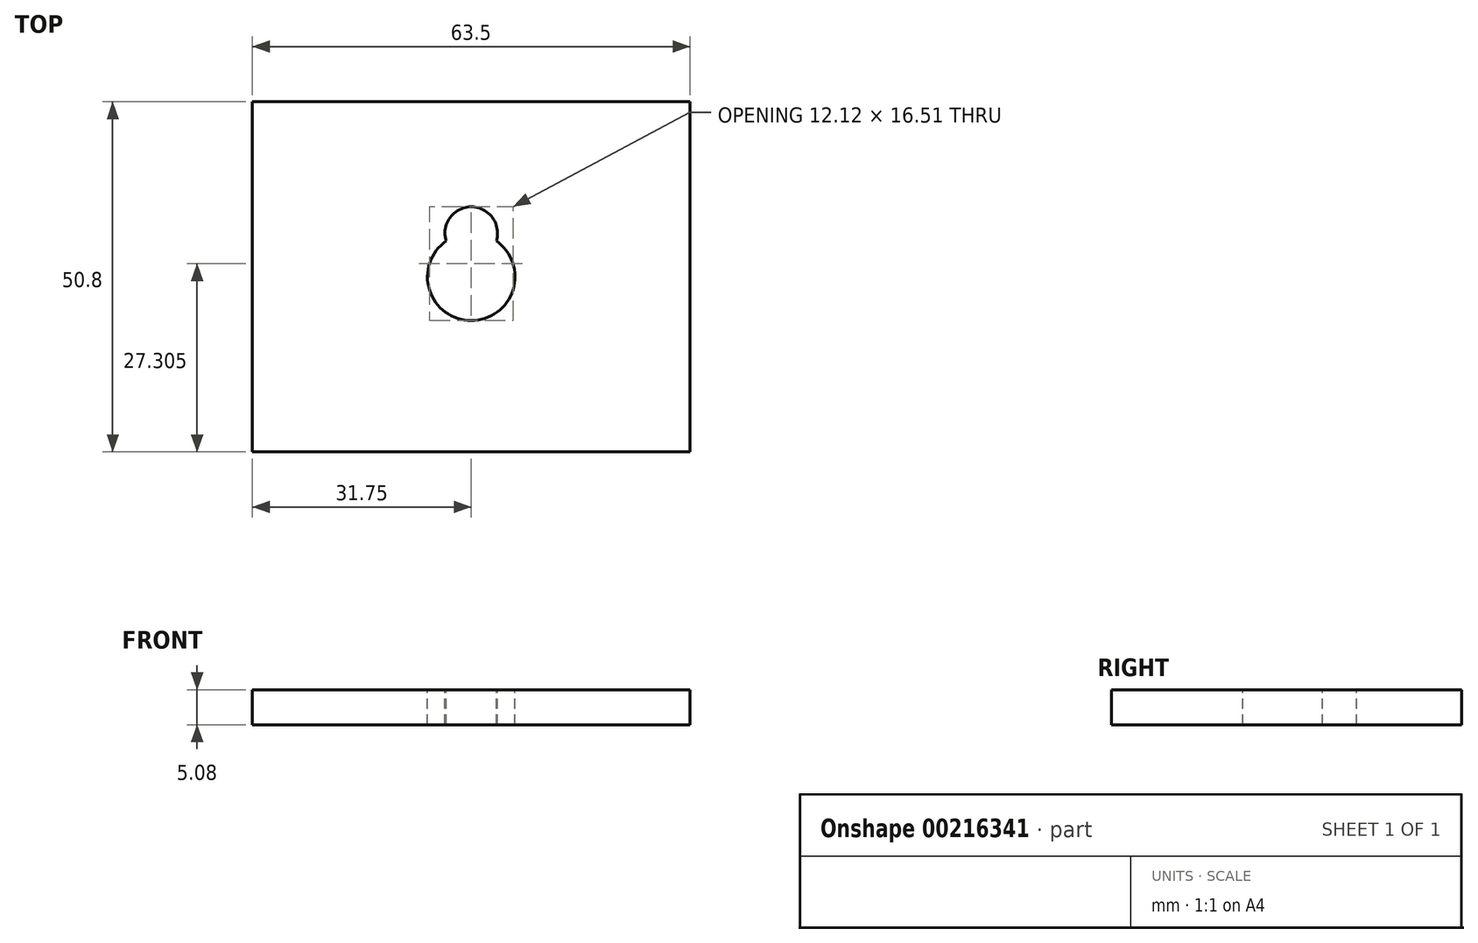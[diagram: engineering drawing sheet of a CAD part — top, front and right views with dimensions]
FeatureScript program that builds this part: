
annotation { "Feature Type Name" : "Feature", "Feature Type Description" : "" }
export const myFeature = defineFeature(function(context is Context, id is Id, definition is map)
    precondition{}
    {
        {
            var Q0;
            Q0=qCreatedBy(makeId("Top.planeOp"),FACE);
            var sketch = newSketch(context, id + "F0", { "sketchPlane" : qUnion([Q0])});
            skLineSegment(sketch, "E0.bottom", {"start": v(-31.75, 25.4) * mm, "end": v(31.75, 25.4) * mm});
            skLineSegment(sketch, "E0.top", {"start": v(-31.75, -25.4) * mm, "end": v(31.75, -25.4) * mm});
            skLineSegment(sketch, "E0.left", {"start": v(-31.75, 25.4) * mm, "end": v(-31.75, -25.4) * mm});
            skLineSegment(sketch, "E0.right", {"start": v(31.75, 25.4) * mm, "end": v(31.75, -25.4) * mm});
            skPoint(sketch, "E0.middle", {"position": v(0, 0) * mm});
            skSolve(sketch);
        }
        {
            var Q0;
            Q0=makeQuery(id+"F0.imprint","IMPRINT",FACE,{"disambiguationData":[TD([[makeQuery(id+"F0.imprint","IMPRINT",EDGE,{"derivedFrom":sQuery(id+"F0.wireOp",EDGE,"E0.bottom")}),-1.0]])]});
            extrude(context, id + "F1", {"entities" : qUnion([Q0]), "depth" : 5.08 * mm});
        }
        {
            var Q0;
            Q0=makeQuery(id+"F1.opExtrude","CAP_FACE",FACE,{"disambiguationData":[OSD([sQuery(id+"F0.wireOp",EDGE,"E0.bottom"),sQuery(id+"F0.wireOp",EDGE,"E0.top"),sQuery(id+"F0.wireOp",EDGE,"E0.left"),sQuery(id+"F0.wireOp",EDGE,"E0.right")])],"isStart":false});
            var sketch = newSketch(context, id + "F2", { "sketchPlane" : qUnion([Q0])});
            skCircle(sketch, "E1", {"center": v(0, 6.35) * mm, "radius": 3.81 * mm});
            skCircle(sketch, "E2", {"center": v(0, 0) * mm, "radius": 6.35 * mm});
            skSolve(sketch);
        }
        {
            var Q0;
            {var subQ0=sQuery(id+"F2.wireOp",EDGE,"E2");var subQ1=sQuery(id+"F2.wireOp",EDGE,"E1");var subQ2=makeQuery(id+"F2.imprint","INTERSECT",VERTEX,{"disambiguationData":[OD(0.0)],"derivedFrom":[subQ1,subQ0]});Q0=makeQuery(id+"F2.imprint","IMPRINT",FACE,{"disambiguationData":[TD([[makeQuery(id+"F2.imprint","IMPRINT",EDGE,{"disambiguationData":[TD([[subQ2,-1.0]])],"derivedFrom":subQ1}),-1.0]])]});}
            var Q1;
            {var subQ0=sQuery(id+"F2.wireOp",EDGE,"E2");var subQ1=sQuery(id+"F2.wireOp",EDGE,"E1");var subQ2=makeQuery(id+"F2.imprint","INTERSECT",VERTEX,{"disambiguationData":[OD(0.0)],"derivedFrom":[subQ1,subQ0]});Q1=makeQuery(id+"F2.imprint","IMPRINT",FACE,{"disambiguationData":[TD([[makeQuery(id+"F2.imprint","IMPRINT",EDGE,{"disambiguationData":[TD([[subQ2,1.0]])],"derivedFrom":subQ1}),1.0]])]});}
            var Q2;
            {var subQ0=sQuery(id+"F2.wireOp",EDGE,"E2");var subQ1=sQuery(id+"F2.wireOp",EDGE,"E1");var subQ2=makeQuery(id+"F2.imprint","INTERSECT",VERTEX,{"disambiguationData":[OD(0.0)],"derivedFrom":[subQ1,subQ0]});Q2=makeQuery(id+"F2.imprint","IMPRINT",FACE,{"disambiguationData":[TD([[makeQuery(id+"F2.imprint","IMPRINT",EDGE,{"disambiguationData":[TD([[subQ2,-1.0]])],"derivedFrom":subQ1}),1.0]])]});}
            extrude(context, id + "F3", {"entities" : qUnion([Q0, Q1, Q2]), "operationType" : NewBodyOperationType.REMOVE, "endBound" : BoundingType.THROUGH_ALL, "oppositeDirection" : true, "depth" : 25.4 * mm});
        }
    });
